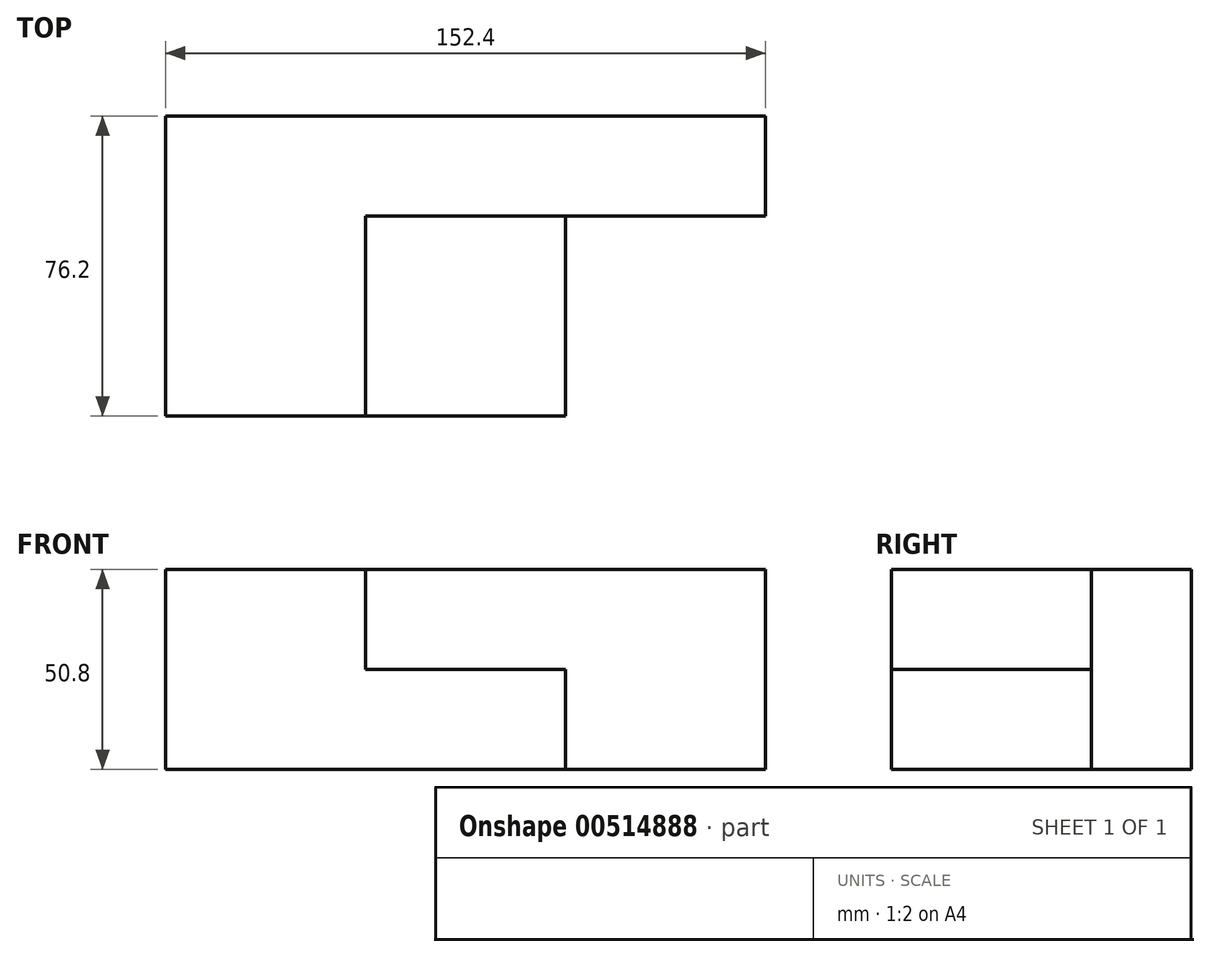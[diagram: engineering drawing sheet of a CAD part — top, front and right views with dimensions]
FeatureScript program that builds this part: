
annotation { "Feature Type Name" : "Feature", "Feature Type Description" : "" }
export const myFeature = defineFeature(function(context is Context, id is Id, definition is map)
    precondition{}
    {
        {
            var Q0;
            Q0=qCreatedBy(makeId("Top.planeOp"),FACE);
            var sketch = newSketch(context, id + "F0", { "sketchPlane" : qUnion([Q0])});
            skLineSegment(sketch, "E0.bottom", {"start": v(-68.78, 86.66) * mm, "end": v(-17.98, 86.66) * mm});
            skLineSegment(sketch, "E0.top", {"start": v(-68.78, 10.46) * mm, "end": v(-17.98, 10.46) * mm});
            skLineSegment(sketch, "E0.left", {"start": v(-68.78, 86.66) * mm, "end": v(-68.78, 10.46) * mm});
            skLineSegment(sketch, "E0.right", {"start": v(-17.98, 86.66) * mm, "end": v(-17.98, 10.46) * mm});
            skLineSegment(sketch, "E1.bottom", {"start": v(-17.98, 61.26) * mm, "end": v(32.82, 61.26) * mm});
            skLineSegment(sketch, "E1.top", {"start": v(-17.98, 10.46) * mm, "end": v(32.82, 10.46) * mm});
            skLineSegment(sketch, "E1.left", {"start": v(-17.98, 61.26) * mm, "end": v(-17.98, 10.46) * mm});
            skLineSegment(sketch, "E1.right", {"start": v(32.82, 61.26) * mm, "end": v(32.82, 10.46) * mm});
            skLineSegment(sketch, "E2.bottom", {"start": v(-17.98, 86.66) * mm, "end": v(83.62, 86.66) * mm});
            skLineSegment(sketch, "E2.top", {"start": v(-17.98, 61.26) * mm, "end": v(83.62, 61.26) * mm});
            skLineSegment(sketch, "E2.left", {"start": v(-17.98, 86.66) * mm, "end": v(-17.98, 61.26) * mm});
            skLineSegment(sketch, "E2.right", {"start": v(83.62, 86.66) * mm, "end": v(83.62, 61.26) * mm});
            skSolve(sketch);
        }
        {
            var Q0;
            Q0=makeQuery(id+"F0.imprint","IMPRINT",FACE,{"disambiguationData":[TD([[makeQuery(id+"F0.imprint","IMPRINT",EDGE,{"derivedFrom":sQuery(id+"F0.wireOp",EDGE,"E1.top")}),1.0]])]});
            extrude(context, id + "F1", {"entities" : qUnion([Q0]), "depth" : 25.4 * mm, "offsetDistance" : 25.4 * mm});
        }
        {
            var Q0;
            Q0=makeQuery(id+"F0.imprint","IMPRINT",FACE,{"disambiguationData":[TD([[makeQuery(id+"F0.imprint","IMPRINT",EDGE,{"derivedFrom":sQuery(id+"F0.wireOp",EDGE,"E0.bottom")}),-1.0]])]});
            var Q1;
            Q1=makeQuery(id+"F0.imprint","IMPRINT",FACE,{"disambiguationData":[TD([[makeQuery(id+"F0.imprint","IMPRINT",EDGE,{"derivedFrom":sQuery(id+"F0.wireOp",EDGE,"E2.bottom")}),-1.0]])]});
            extrude(context, id + "F2", {"entities" : qUnion([Q0, Q1]), "operationType" : NewBodyOperationType.ADD, "depth" : 50.8 * mm, "offsetDistance" : 25.4 * mm});
        }
    });
